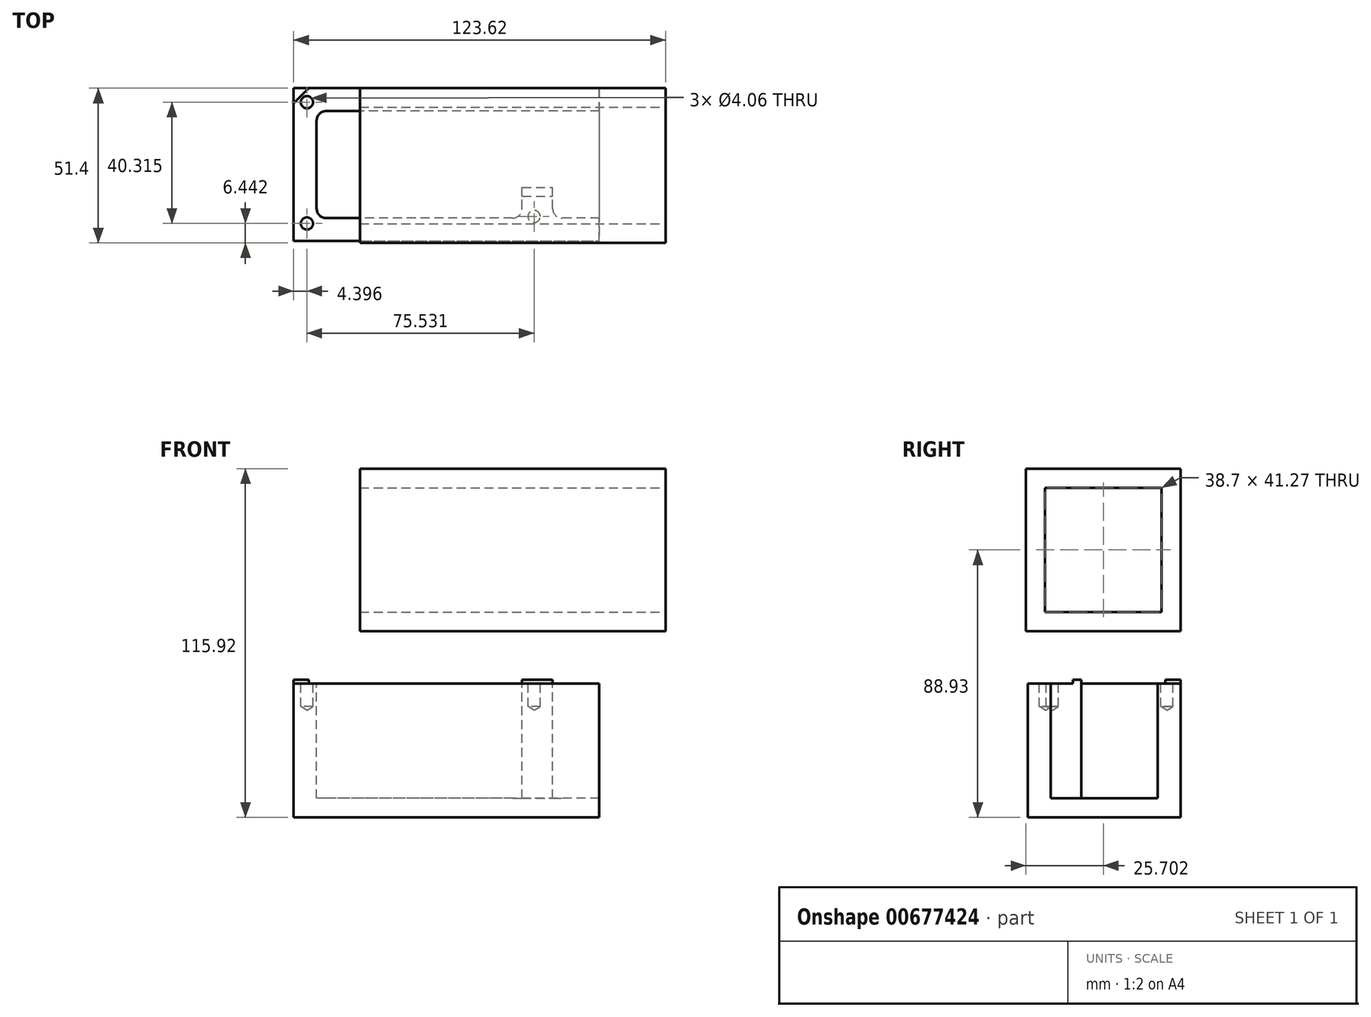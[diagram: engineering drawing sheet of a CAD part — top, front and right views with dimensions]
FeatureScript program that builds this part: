
annotation { "Feature Type Name" : "Feature", "Feature Type Description" : "" }
export const myFeature = defineFeature(function(context is Context, id is Id, definition is map)
    precondition{}
    {
        {
            var Q0;
            Q0=qCreatedBy(makeId("Top.planeOp"),FACE);
            var sketch = newSketch(context, id + "F0", { "sketchPlane" : qUnion([Q0])});
            skLineSegment(sketch, "E0.bottom", {"start": v(-72.82, -50.8) * mm, "end": v(28.78, -50.8) * mm});
            skLineSegment(sketch, "E0.top", {"start": v(-72.82, 0) * mm, "end": v(28.78, 0) * mm});
            skLineSegment(sketch, "E0.left", {"start": v(-72.82, -50.8) * mm, "end": v(-72.82, 0) * mm});
            skLineSegment(sketch, "E0.right", {"start": v(28.78, -50.8) * mm, "end": v(28.78, -43.18) * mm});
            skLineSegment(sketch, "E1.bottom", {"start": v(28.78, -43.18) * mm, "end": v(16.45, -43.18) * mm});
            skLineSegment(sketch, "E1.top", {"start": v(28.78, -7.62) * mm, "end": v(-62.02, -7.62) * mm});
            skLineSegment(sketch, "E1.right", {"start": v(-65.2, -40) * mm, "end": v(-65.2, -10.8) * mm});
            skLineSegment(sketch, "E2.trimOffspring", {"start": v(28.78, -7.62) * mm, "end": v(28.78, 0) * mm});
            skPoint(sketch, "E3.visualSharp", {"position": v(-65.2, -43.18) * mm});
            skArc(sketch, "E3.filletArc", {"start": v(-65.2, -40) * mm, "mid": v(-64.27, -42.25) * mm, "end": v(-62.02, -43.18) * mm});
            skPoint(sketch, "E4.visualSharp", {"position": v(-65.2, -7.62) * mm});
            skArc(sketch, "E4.filletArc", {"start": v(-62.02, -7.62) * mm, "mid": v(-64.27, -8.55) * mm, "end": v(-65.2, -10.8) * mm});
            skLineSegment(sketch, "E5.top", {"start": v(3.11, -33.02) * mm, "end": v(13.27, -33.02) * mm});
            skLineSegment(sketch, "E5.left", {"start": v(3.11, -40) * mm, "end": v(3.11, -33.02) * mm});
            skLineSegment(sketch, "E5.right", {"start": v(13.27, -40) * mm, "end": v(13.27, -33.02) * mm});
            skLineSegment(sketch, "E6.trimOffspring", {"start": v(-0.06, -43.18) * mm, "end": v(-62.02, -43.18) * mm});
            skPoint(sketch, "E7.visualSharp", {"position": v(3.11, -43.18) * mm});
            skArc(sketch, "E7.filletArc", {"start": v(-0.06, -43.18) * mm, "mid": v(2.18, -42.25) * mm, "end": v(3.11, -40) * mm});
            skPoint(sketch, "E8.visualSharp", {"position": v(13.27, -43.18) * mm});
            skArc(sketch, "E8.filletArc", {"start": v(13.27, -40) * mm, "mid": v(14.2, -42.25) * mm, "end": v(16.45, -43.18) * mm});
            skSolve(sketch);
        }
        {
            var Q0;
            Q0=makeQuery(id+"F0.imprint","IMPRINT",FACE,{"disambiguationData":[TD([[makeQuery(id+"F0.imprint","IMPRINT",EDGE,{"derivedFrom":sQuery(id+"F0.wireOp",EDGE,"E0.bottom")}),1.0]])]});
            extrude(context, id + "F1", {"entities" : qUnion([Q0]), "oppositeDirection" : true, "depth" : 38.1 * mm, "offsetDistance" : 25.4 * mm});
        }
        {
            var Q0;
            Q0=makeQuery(id+"F1.opExtrude","CAP_FACE",FACE,{"disambiguationData":[OSD([sQuery(id+"F0.wireOp",EDGE,"E0.bottom"),sQuery(id+"F0.wireOp",EDGE,"E0.top"),sQuery(id+"F0.wireOp",EDGE,"E0.left"),sQuery(id+"F0.wireOp",EDGE,"E0.right"),sQuery(id+"F0.wireOp",EDGE,"E1.bottom"),sQuery(id+"F0.wireOp",EDGE,"E1.top"),sQuery(id+"F0.wireOp",EDGE,"E1.right"),sQuery(id+"F0.wireOp",EDGE,"E2.trimOffspring"),sQuery(id+"F0.wireOp",EDGE,"E3.filletArc"),sQuery(id+"F0.wireOp",EDGE,"E4.filletArc"),sQuery(id+"F0.wireOp",EDGE,"E5.top"),sQuery(id+"F0.wireOp",EDGE,"E5.left"),sQuery(id+"F0.wireOp",EDGE,"E5.right"),sQuery(id+"F0.wireOp",EDGE,"E6.trimOffspring"),sQuery(id+"F0.wireOp",EDGE,"E7.filletArc"),sQuery(id+"F0.wireOp",EDGE,"E8.filletArc")])],"isStart":false});
            var sketch = newSketch(context, id + "F2", { "sketchPlane" : qUnion([Q0])});
            skLineSegment(sketch, "E9", {"start": v(28.78, 0) * mm, "end": v(28.78, 50.8) * mm});
            skLineSegment(sketch, "E10", {"start": v(28.78, 50.8) * mm, "end": v(-72.82, 50.8) * mm});
            skLineSegment(sketch, "E11", {"start": v(-72.82, 50.8) * mm, "end": v(-72.82, 0) * mm});
            skLineSegment(sketch, "E12", {"start": v(-72.82, 0) * mm, "end": v(28.78, 0) * mm});
            skSolve(sketch);
        }
        {
            var Q0;
            Q0 = qSketchRegion(id + "F2", true);
            extrude(context, id + "F3", {"entities" : qUnion([Q0]), "operationType" : NewBodyOperationType.ADD, "depth" : 6.35 * mm, "offsetDistance" : 25.4 * mm});
        }
        {
            var Q0;
            Q0=makeQuery(id+"F0.imprint","IMPRINT",FACE,{"disambiguationData":[TD([[makeQuery(id+"F0.imprint","IMPRINT",EDGE,{"derivedFrom":sQuery(id+"F0.wireOp",EDGE,"E0.bottom")}),1.0]])]});
            var sketch = newSketch(context, id + "F4", { "sketchPlane" : qUnion([Q0])});
            skLineSegment(sketch, "E13", {"start": v(-72.82, -5.08) * mm, "end": v(-67.74, 0) * mm});
            skLineSegment(sketch, "E14", {"start": v(-67.74, 0) * mm, "end": v(-72.82, 0) * mm});
            skLineSegment(sketch, "E15", {"start": v(-72.82, 0) * mm, "end": v(-72.82, -5.08) * mm});
            skLineSegment(sketch, "E16.bottom", {"start": v(3.11, -33.02) * mm, "end": v(13.27, -33.02) * mm});
            skLineSegment(sketch, "E16.top", {"start": v(3.11, -35.85) * mm, "end": v(13.27, -35.85) * mm});
            skLineSegment(sketch, "E16.left", {"start": v(3.11, -33.02) * mm, "end": v(3.11, -35.85) * mm});
            skLineSegment(sketch, "E16.right", {"start": v(13.27, -33.02) * mm, "end": v(13.27, -35.85) * mm});
            skSolve(sketch);
        }
        {
            var Q0;
            Q0 = qSketchRegion(id + "F4", true);
            extrude(context, id + "F5", {"entities" : qUnion([Q0]), "operationType" : NewBodyOperationType.ADD, "depth" : 1.3 * mm, "offsetDistance" : 25.4 * mm});
        }
        {
            var Q0;
            Q0=makeQuery(id+"F0.imprint","IMPRINT",FACE,{"disambiguationData":[TD([[makeQuery(id+"F0.imprint","IMPRINT",EDGE,{"derivedFrom":sQuery(id+"F0.wireOp",EDGE,"E0.bottom")}),1.0]])]});
            var sketch = newSketch(context, id + "F6", { "sketchPlane" : qUnion([Q0])});
            skLineSegment(sketch, "E17", {"start": v(-68.42, -4.64) * mm, "end": v(-68.42, -44.96) * mm});
            skLineSegment(sketch, "E18", {"start": v(7.1, -42.63) * mm, "end": v(7.1, -3.86) * mm});
            skSolve(sketch);
        }
        {
            var Q0;
            Q0=sQuery(id+"F6.wireOp",VERTEX,"E17.start");
            var Q1;
            Q1=sQuery(id+"F6.wireOp",VERTEX,"E17.end");
            var Q2;
            Q2=sQuery(id+"F6.wireOp",VERTEX,"E18.start");
            var Q3;
            Q3=makeQuery(id+"F1.opExtrude","SWEPT_BODY",BODY,{"disambiguationData":[OSD([sQuery(id+"F0.wireOp",EDGE,"E0.bottom"),sQuery(id+"F0.wireOp",EDGE,"E0.top"),sQuery(id+"F0.wireOp",EDGE,"E0.left"),sQuery(id+"F0.wireOp",EDGE,"E0.right"),sQuery(id+"F0.wireOp",EDGE,"E1.bottom"),sQuery(id+"F0.wireOp",EDGE,"E1.top"),sQuery(id+"F0.wireOp",EDGE,"E1.right"),sQuery(id+"F0.wireOp",EDGE,"E2.trimOffspring"),sQuery(id+"F0.wireOp",EDGE,"E3.filletArc"),sQuery(id+"F0.wireOp",EDGE,"E4.filletArc"),sQuery(id+"F0.wireOp",EDGE,"E5.top"),sQuery(id+"F0.wireOp",EDGE,"E5.left"),sQuery(id+"F0.wireOp",EDGE,"E5.right"),sQuery(id+"F0.wireOp",EDGE,"E6.trimOffspring"),sQuery(id+"F0.wireOp",EDGE,"E7.filletArc"),sQuery(id+"F0.wireOp",EDGE,"E8.filletArc")])]});
            hole(context, id + "F7", {"style" : HoleStyle.SIMPLE, "endStyle" : HoleEndStyle.BLIND, "holeDiameter" : 4.06 * mm, "majorDiameter" : 6.35 * mm, "holeDepth" : 7.62 * mm, "isTappedThrough" : true, "tappedDepth" : 12.7 * mm, "tapClearance" : 3, "startFromSketch" : true, "locations" : qUnion([Q0, Q1, Q2]), "scope" : qUnion([Q3])});
        }
        {
            var Q0;
            Q0=qCreatedBy(makeId("Right.planeOp"),FACE);
            var sketch = newSketch(context, id + "F8", { "sketchPlane" : qUnion([Q0])});
            skLineSegment(sketch, "E19.bottom", {"start": v(-51.4, 17.5) * mm, "end": v(0, 17.5) * mm});
            skLineSegment(sketch, "E19.top", {"start": v(-51.4, 71.47) * mm, "end": v(0, 71.47) * mm});
            skLineSegment(sketch, "E19.left", {"start": v(-51.4, 17.5) * mm, "end": v(-51.4, 71.47) * mm});
            skLineSegment(sketch, "E19.right", {"start": v(0, 17.5) * mm, "end": v(0, 71.47) * mm});
            skSolve(sketch);
        }
        {
            var Q0;
            Q0=makeQuery(id+"F8.imprint","IMPRINT",FACE,{"disambiguationData":[TD([[makeQuery(id+"F8.imprint","IMPRINT",EDGE,{"derivedFrom":sQuery(id+"F8.wireOp",EDGE,"E19.bottom")}),1.0]])]});
            extrude(context, id + "F9", {"entities" : qUnion([Q0]), "oppositeDirection" : true, "depth" : 50.8 * mm, "offsetDistance" : 25.4 * mm, "hasSecondDirection" : true, "secondDirectionOppositeDirection" : false, "secondDirectionDepth" : 50.8 * mm});
        }
        {
            var Q0;
            Q0=makeQuery(id+"F9.opExtrude","CAP_FACE",FACE,{"disambiguationData":[OSD([sQuery(id+"F8.wireOp",EDGE,"E19.bottom"),sQuery(id+"F8.wireOp",EDGE,"E19.top"),sQuery(id+"F8.wireOp",EDGE,"E19.left"),sQuery(id+"F8.wireOp",EDGE,"E19.right")])],"isStart":true});
            var Q1;
            Q1=makeQuery(id+"F9.opExtrude","CAP_FACE",FACE,{"disambiguationData":[OSD([sQuery(id+"F8.wireOp",EDGE,"E19.bottom"),sQuery(id+"F8.wireOp",EDGE,"E19.top"),sQuery(id+"F8.wireOp",EDGE,"E19.left"),sQuery(id+"F8.wireOp",EDGE,"E19.right")])],"isStart":false});
            shell(context, id + "F10", {"entities" : qUnion([Q0, Q1]), "thickness" : 6.35 * mm});
        }
    });
